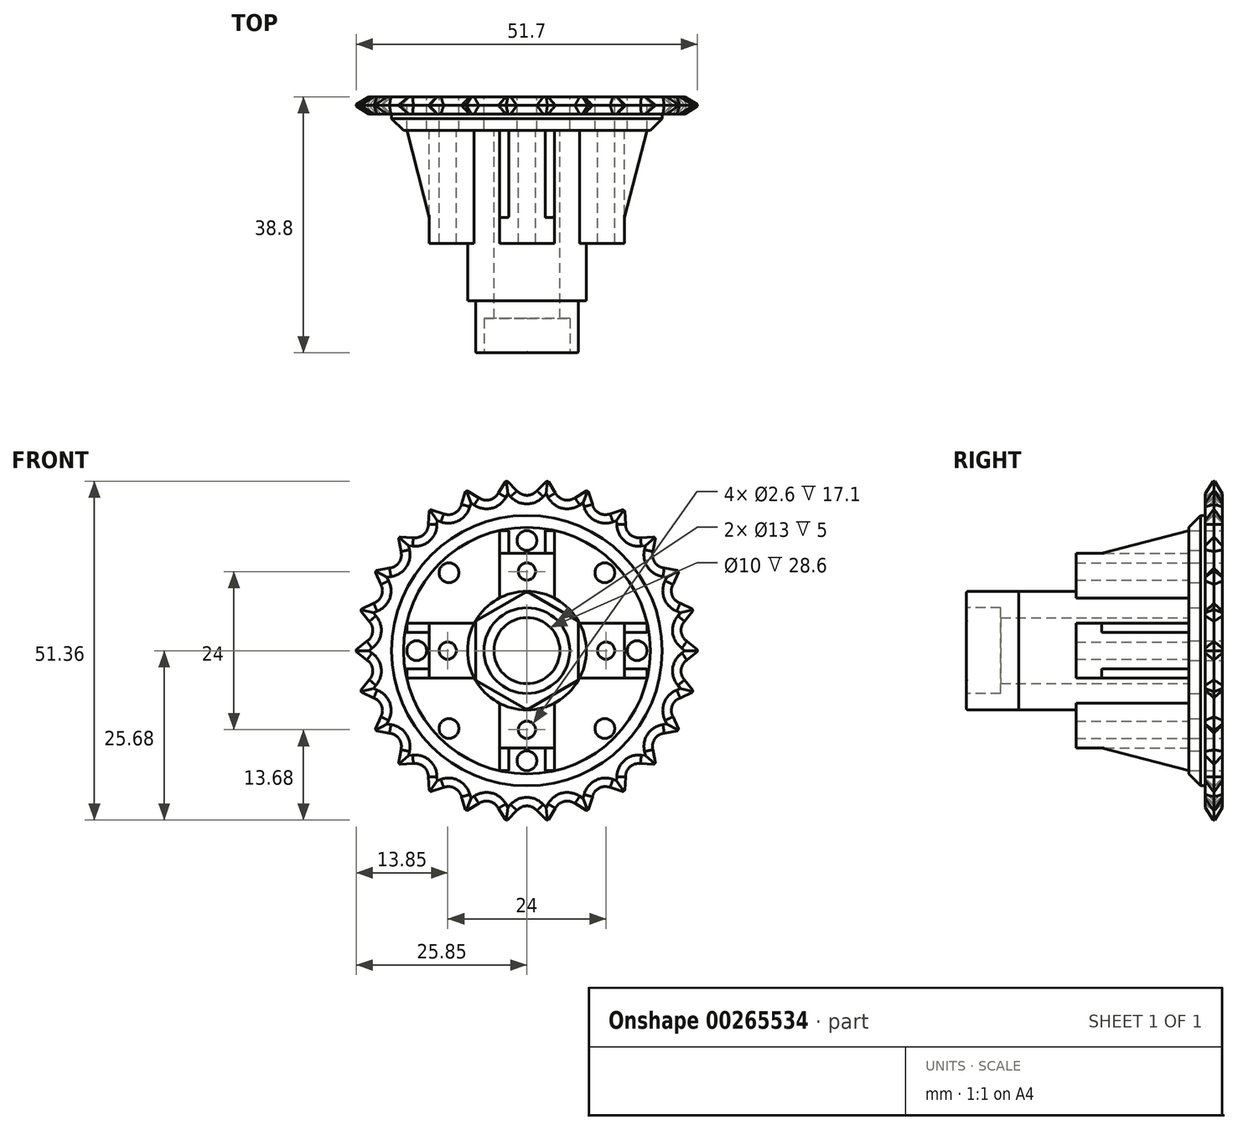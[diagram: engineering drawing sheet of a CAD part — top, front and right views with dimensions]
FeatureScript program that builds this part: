
annotation { "Feature Type Name" : "Feature", "Feature Type Description" : "" }
export const myFeature = defineFeature(function(context is Context, id is Id, definition is map)
    precondition{}
    {
        {
            var Q0;
            Q0=qCreatedBy(makeId("Front.planeOp"),FACE);
            var sketch = newSketch(context, id + "F0", { "sketchPlane" : qUnion([Q0])});
            skCircle(sketch, "E0", {"center": v(0, 0) * mm, "radius": 22.85 * mm});
            skSolve(sketch);
        }
        {
            var Q0;
            Q0=makeQuery(id+"F0.imprint","IMPRINT",FACE,{"disambiguationData":[TD([[makeQuery(id+"F0.imprint","IMPRINT",EDGE,{"derivedFrom":sQuery(id+"F0.wireOp",EDGE,"E0")}),1.0]])]});
            extrude(context, id + "F1", {"entities" : qUnion([Q0]), "depth" : 2.6 * mm});
        }
        {
            var Q0;
            Q0=qCreatedBy(makeId("Front.planeOp"),FACE);
            var sketch = newSketch(context, id + "F2", { "sketchPlane" : qUnion([Q0])});
            skCircle(sketch, "E1", {"center": v(0, 0) * mm, "radius": 25.85 * mm});
            skLineSegment(sketch, "E2", {"start": v(0, 0) * mm, "end": v(0, 38.8) * mm, "construction": true});
            skPoint(sketch, "E3.center", {"position": v(0, 0.05) * mm});
            skLineSegment(sketch, "E4", {"start": v(0, 25.85) * mm, "end": v(-3.12, 25.85) * mm, "construction": true});
            skLineSegment(sketch, "E5", {"start": v(0, 25.85) * mm, "end": v(3.12, 25.85) * mm, "construction": true});
            skLineSegment(sketch, "E6", {"start": v(-3.12, 25.85) * mm, "end": v(-3.12, 22.64) * mm, "construction": true});
            skLineSegment(sketch, "E7", {"start": v(3.12, 25.85) * mm, "end": v(3.12, 22.64) * mm, "construction": true});
            skLineSegment(sketch, "E8", {"start": v(-3.12, 25.85) * mm, "end": v(0, 22.73) * mm});
            skLineSegment(sketch, "E9", {"start": v(3.12, 25.85) * mm, "end": v(0, 22.73) * mm});
            skLineSegment(sketch, "E10", {"start": v(-3.12, 24.24) * mm, "end": v(3.12, 24.24) * mm, "construction": true});
            skArc(sketch, "E11", {"start": v(-1.52, 24.24) * mm, "mid": v(0, 23.55) * mm, "end": v(1.52, 24.24) * mm});
            skLineSegment(sketch, "E12.1.0", {"start": v(-9.22, 24.35) * mm, "end": v(-5.44, 22.07) * mm});
            skArc(sketch, "E12.1.1", {"start": v(-7.27, 23.18) * mm, "mid": v(-5.64, 22.87) * mm, "end": v(-4.33, 23.9) * mm});
            skLineSegment(sketch, "E12.1.2", {"start": v(-3.15, 25.85) * mm, "end": v(-5.44, 22.07) * mm});
            skLineSegment(sketch, "E12.2.0", {"start": v(-14.78, 21.44) * mm, "end": v(-10.56, 20.12) * mm});
            skArc(sketch, "E12.2.1", {"start": v(-12.6, 20.76) * mm, "mid": v(-10.94, 20.85) * mm, "end": v(-9.92, 22.17) * mm});
            skLineSegment(sketch, "E12.2.2", {"start": v(-9.25, 24.34) * mm, "end": v(-10.56, 20.12) * mm});
            skLineSegment(sketch, "E12.3.0", {"start": v(-19.48, 17.28) * mm, "end": v(-15.07, 17.01) * mm});
            skArc(sketch, "E12.3.1", {"start": v(-17.21, 17.14) * mm, "mid": v(-15.62, 17.63) * mm, "end": v(-14.94, 19.15) * mm});
            skLineSegment(sketch, "E12.3.2", {"start": v(-14.8, 21.42) * mm, "end": v(-15.07, 17.01) * mm});
            skLineSegment(sketch, "E12.4.0", {"start": v(-23.05, 12.11) * mm, "end": v(-18.7, 12.91) * mm});
            skArc(sketch, "E12.4.1", {"start": v(-20.81, 12.52) * mm, "mid": v(-19.38, 13.38) * mm, "end": v(-19.1, 15.02) * mm});
            skLineSegment(sketch, "E12.4.2", {"start": v(-19.5, 17.26) * mm, "end": v(-18.7, 12.91) * mm});
            skLineSegment(sketch, "E12.5.0", {"start": v(-25.28, 6.25) * mm, "end": v(-21.25, 8.06) * mm});
            skArc(sketch, "E12.5.1", {"start": v(-23.2, 7.18) * mm, "mid": v(-22.02, 8.35) * mm, "end": v(-22.13, 10.01) * mm});
            skLineSegment(sketch, "E12.5.2", {"start": v(-23.06, 12.09) * mm, "end": v(-21.25, 8.06) * mm});
            skLineSegment(sketch, "E12.6.0", {"start": v(-26.04, 0.02) * mm, "end": v(-22.56, 2.74) * mm});
            skArc(sketch, "E12.6.1", {"start": v(-24.25, 1.42) * mm, "mid": v(-23.38, 2.84) * mm, "end": v(-23.88, 4.43) * mm});
            skLineSegment(sketch, "E12.6.2", {"start": v(-25.29, 6.22) * mm, "end": v(-22.56, 2.74) * mm});
            skLineSegment(sketch, "E12.7.0", {"start": v(-25.29, -6.22) * mm, "end": v(-22.56, -2.74) * mm});
            skArc(sketch, "E12.7.1", {"start": v(-23.88, -4.43) * mm, "mid": v(-23.38, -2.84) * mm, "end": v(-24.25, -1.42) * mm});
            skLineSegment(sketch, "E12.7.2", {"start": v(-26.04, -0.02) * mm, "end": v(-22.56, -2.74) * mm});
            skLineSegment(sketch, "E12.8.0", {"start": v(-23.06, -12.09) * mm, "end": v(-21.25, -8.06) * mm});
            skArc(sketch, "E12.8.1", {"start": v(-22.13, -10.01) * mm, "mid": v(-22.02, -8.35) * mm, "end": v(-23.2, -7.18) * mm});
            skLineSegment(sketch, "E12.8.2", {"start": v(-25.28, -6.25) * mm, "end": v(-21.25, -8.06) * mm});
            skLineSegment(sketch, "E12.9.0", {"start": v(-19.5, -17.26) * mm, "end": v(-18.7, -12.91) * mm});
            skArc(sketch, "E12.9.1", {"start": v(-19.1, -15.02) * mm, "mid": v(-19.38, -13.38) * mm, "end": v(-20.81, -12.52) * mm});
            skLineSegment(sketch, "E12.9.2", {"start": v(-23.05, -12.11) * mm, "end": v(-18.7, -12.91) * mm});
            skLineSegment(sketch, "E12.10.0", {"start": v(-14.8, -21.42) * mm, "end": v(-15.07, -17.01) * mm});
            skArc(sketch, "E12.10.1", {"start": v(-14.94, -19.15) * mm, "mid": v(-15.62, -17.63) * mm, "end": v(-17.21, -17.14) * mm});
            skLineSegment(sketch, "E12.10.2", {"start": v(-19.48, -17.28) * mm, "end": v(-15.07, -17.01) * mm});
            skLineSegment(sketch, "E12.11.0", {"start": v(-9.25, -24.34) * mm, "end": v(-10.56, -20.12) * mm});
            skArc(sketch, "E12.11.1", {"start": v(-9.92, -22.17) * mm, "mid": v(-10.94, -20.85) * mm, "end": v(-12.6, -20.76) * mm});
            skLineSegment(sketch, "E12.11.2", {"start": v(-14.78, -21.44) * mm, "end": v(-10.56, -20.12) * mm});
            skLineSegment(sketch, "E12.12.0", {"start": v(-3.15, -25.85) * mm, "end": v(-5.44, -22.07) * mm});
            skArc(sketch, "E12.12.1", {"start": v(-4.33, -23.9) * mm, "mid": v(-5.64, -22.87) * mm, "end": v(-7.27, -23.18) * mm});
            skLineSegment(sketch, "E12.12.2", {"start": v(-9.22, -24.35) * mm, "end": v(-5.44, -22.07) * mm});
            skLineSegment(sketch, "E12.13.0", {"start": v(3.12, -25.85) * mm, "end": v(0, -22.73) * mm});
            skArc(sketch, "E12.13.1", {"start": v(1.52, -24.24) * mm, "mid": v(0, -23.55) * mm, "end": v(-1.52, -24.24) * mm});
            skLineSegment(sketch, "E12.13.2", {"start": v(-3.12, -25.85) * mm, "end": v(0, -22.73) * mm});
            skLineSegment(sketch, "E12.14.0", {"start": v(9.22, -24.35) * mm, "end": v(5.44, -22.07) * mm});
            skArc(sketch, "E12.14.1", {"start": v(7.27, -23.18) * mm, "mid": v(5.64, -22.87) * mm, "end": v(4.33, -23.9) * mm});
            skLineSegment(sketch, "E12.14.2", {"start": v(3.15, -25.85) * mm, "end": v(5.44, -22.07) * mm});
            skLineSegment(sketch, "E12.15.0", {"start": v(14.78, -21.44) * mm, "end": v(10.56, -20.12) * mm});
            skArc(sketch, "E12.15.1", {"start": v(12.6, -20.76) * mm, "mid": v(10.94, -20.85) * mm, "end": v(9.92, -22.17) * mm});
            skLineSegment(sketch, "E12.15.2", {"start": v(9.25, -24.34) * mm, "end": v(10.56, -20.12) * mm});
            skLineSegment(sketch, "E12.16.0", {"start": v(19.48, -17.28) * mm, "end": v(15.07, -17.01) * mm});
            skArc(sketch, "E12.16.1", {"start": v(17.21, -17.14) * mm, "mid": v(15.62, -17.63) * mm, "end": v(14.94, -19.15) * mm});
            skLineSegment(sketch, "E12.16.2", {"start": v(14.8, -21.42) * mm, "end": v(15.07, -17.01) * mm});
            skLineSegment(sketch, "E12.17.0", {"start": v(23.05, -12.11) * mm, "end": v(18.7, -12.91) * mm});
            skArc(sketch, "E12.17.1", {"start": v(20.81, -12.52) * mm, "mid": v(19.38, -13.38) * mm, "end": v(19.1, -15.02) * mm});
            skLineSegment(sketch, "E12.17.2", {"start": v(19.5, -17.26) * mm, "end": v(18.7, -12.91) * mm});
            skLineSegment(sketch, "E12.18.0", {"start": v(25.28, -6.25) * mm, "end": v(21.25, -8.06) * mm});
            skArc(sketch, "E12.18.1", {"start": v(23.2, -7.18) * mm, "mid": v(22.02, -8.35) * mm, "end": v(22.13, -10.01) * mm});
            skLineSegment(sketch, "E12.18.2", {"start": v(23.06, -12.09) * mm, "end": v(21.25, -8.06) * mm});
            skLineSegment(sketch, "E12.19.0", {"start": v(26.04, -0.02) * mm, "end": v(22.56, -2.74) * mm});
            skArc(sketch, "E12.19.1", {"start": v(24.25, -1.42) * mm, "mid": v(23.38, -2.84) * mm, "end": v(23.88, -4.43) * mm});
            skLineSegment(sketch, "E12.19.2", {"start": v(25.29, -6.22) * mm, "end": v(22.56, -2.74) * mm});
            skLineSegment(sketch, "E12.20.0", {"start": v(25.29, 6.22) * mm, "end": v(22.56, 2.74) * mm});
            skArc(sketch, "E12.20.1", {"start": v(23.88, 4.43) * mm, "mid": v(23.38, 2.84) * mm, "end": v(24.25, 1.42) * mm});
            skLineSegment(sketch, "E12.20.2", {"start": v(26.04, 0.02) * mm, "end": v(22.56, 2.74) * mm});
            skLineSegment(sketch, "E12.21.0", {"start": v(23.06, 12.09) * mm, "end": v(21.25, 8.06) * mm});
            skArc(sketch, "E12.21.1", {"start": v(22.13, 10.01) * mm, "mid": v(22.02, 8.35) * mm, "end": v(23.2, 7.18) * mm});
            skLineSegment(sketch, "E12.21.2", {"start": v(25.28, 6.25) * mm, "end": v(21.25, 8.06) * mm});
            skLineSegment(sketch, "E12.22.0", {"start": v(19.5, 17.26) * mm, "end": v(18.7, 12.91) * mm});
            skArc(sketch, "E12.22.1", {"start": v(19.1, 15.02) * mm, "mid": v(19.38, 13.38) * mm, "end": v(20.81, 12.52) * mm});
            skLineSegment(sketch, "E12.22.2", {"start": v(23.05, 12.11) * mm, "end": v(18.7, 12.91) * mm});
            skLineSegment(sketch, "E12.23.0", {"start": v(14.8, 21.42) * mm, "end": v(15.07, 17.01) * mm});
            skArc(sketch, "E12.23.1", {"start": v(14.94, 19.15) * mm, "mid": v(15.62, 17.63) * mm, "end": v(17.21, 17.14) * mm});
            skLineSegment(sketch, "E12.23.2", {"start": v(19.48, 17.28) * mm, "end": v(15.07, 17.01) * mm});
            skLineSegment(sketch, "E12.24.0", {"start": v(9.25, 24.34) * mm, "end": v(10.56, 20.12) * mm});
            skArc(sketch, "E12.24.1", {"start": v(9.92, 22.17) * mm, "mid": v(10.94, 20.85) * mm, "end": v(12.6, 20.76) * mm});
            skLineSegment(sketch, "E12.24.2", {"start": v(14.78, 21.44) * mm, "end": v(10.56, 20.12) * mm});
            skLineSegment(sketch, "E12.25.0", {"start": v(3.15, 25.85) * mm, "end": v(5.44, 22.07) * mm});
            skArc(sketch, "E12.25.1", {"start": v(4.33, 23.9) * mm, "mid": v(5.64, 22.87) * mm, "end": v(7.27, 23.18) * mm});
            skLineSegment(sketch, "E12.25.2", {"start": v(9.22, 24.35) * mm, "end": v(5.44, 22.07) * mm});
            skSolve(sketch);
        }
        {
            var Q0;
            {var subQ21=sQuery(id+"F2.wireOp",EDGE,"E1");var subQ92=sQuery(id+"F2.wireOp",EDGE,"E12.20.0");var subQ115=makeQuery(id+"F2.imprint","INTERSECT",VERTEX,{"derivedFrom":[subQ21,subQ92]});Q0=makeQuery(id+"F2.imprint","IMPRINT",FACE,{"disambiguationData":[TD([[makeQuery(id+"F2.imprint","IMPRINT",EDGE,{"disambiguationData":[TD([[subQ115,-1.0]])],"derivedFrom":subQ21}),1.0]])]});}
            var Q1;
            {var subQ0=sQuery(id+"F2.wireOp",EDGE,"E12.1.2");var subQ1=sQuery(id+"F2.wireOp",EDGE,"E12.1.0");var subQ2=makeQuery(id+"F2.imprint","INTERSECT",VERTEX,{"derivedFrom":[subQ1,subQ0]});Q1=makeQuery(id+"F2.imprint","IMPRINT",FACE,{"disambiguationData":[TD([[makeQuery(id+"F2.imprint","IMPRINT",EDGE,{"disambiguationData":[TD([[subQ2,1.0]])],"derivedFrom":subQ1}),1.0]])]});}
            var Q2;
            {var subQ0=sQuery(id+"F2.wireOp",EDGE,"E9");var subQ1=sQuery(id+"F2.wireOp",EDGE,"E8");var subQ2=makeQuery(id+"F2.imprint","INTERSECT",VERTEX,{"derivedFrom":[subQ1,subQ0]});Q2=makeQuery(id+"F2.imprint","IMPRINT",FACE,{"disambiguationData":[TD([[makeQuery(id+"F2.imprint","IMPRINT",EDGE,{"disambiguationData":[TD([[subQ2,1.0]])],"derivedFrom":subQ1}),1.0]])]});}
            var Q3;
            {var subQ0=sQuery(id+"F2.wireOp",EDGE,"E12.25.2");var subQ1=sQuery(id+"F2.wireOp",EDGE,"E12.25.0");var subQ2=makeQuery(id+"F2.imprint","INTERSECT",VERTEX,{"derivedFrom":[subQ1,subQ0]});Q3=makeQuery(id+"F2.imprint","IMPRINT",FACE,{"disambiguationData":[TD([[makeQuery(id+"F2.imprint","IMPRINT",EDGE,{"disambiguationData":[TD([[subQ2,1.0]])],"derivedFrom":subQ1}),1.0]])]});}
            var Q4;
            {var subQ0=sQuery(id+"F2.wireOp",EDGE,"E12.24.2");var subQ1=sQuery(id+"F2.wireOp",EDGE,"E12.24.0");var subQ2=makeQuery(id+"F2.imprint","INTERSECT",VERTEX,{"derivedFrom":[subQ1,subQ0]});Q4=makeQuery(id+"F2.imprint","IMPRINT",FACE,{"disambiguationData":[TD([[makeQuery(id+"F2.imprint","IMPRINT",EDGE,{"disambiguationData":[TD([[subQ2,1.0]])],"derivedFrom":subQ1}),1.0]])]});}
            var Q5;
            {var subQ0=sQuery(id+"F2.wireOp",EDGE,"E12.23.2");var subQ1=sQuery(id+"F2.wireOp",EDGE,"E12.23.0");var subQ2=makeQuery(id+"F2.imprint","INTERSECT",VERTEX,{"derivedFrom":[subQ1,subQ0]});Q5=makeQuery(id+"F2.imprint","IMPRINT",FACE,{"disambiguationData":[TD([[makeQuery(id+"F2.imprint","IMPRINT",EDGE,{"disambiguationData":[TD([[subQ2,1.0]])],"derivedFrom":subQ1}),1.0]])]});}
            var Q6;
            {var subQ0=sQuery(id+"F2.wireOp",EDGE,"E12.22.2");var subQ1=sQuery(id+"F2.wireOp",EDGE,"E12.22.0");var subQ2=makeQuery(id+"F2.imprint","INTERSECT",VERTEX,{"derivedFrom":[subQ1,subQ0]});Q6=makeQuery(id+"F2.imprint","IMPRINT",FACE,{"disambiguationData":[TD([[makeQuery(id+"F2.imprint","IMPRINT",EDGE,{"disambiguationData":[TD([[subQ2,1.0]])],"derivedFrom":subQ1}),1.0]])]});}
            var Q7;
            {var subQ0=sQuery(id+"F2.wireOp",EDGE,"E12.2.2");var subQ1=sQuery(id+"F2.wireOp",EDGE,"E12.2.0");var subQ2=makeQuery(id+"F2.imprint","INTERSECT",VERTEX,{"derivedFrom":[subQ1,subQ0]});Q7=makeQuery(id+"F2.imprint","IMPRINT",FACE,{"disambiguationData":[TD([[makeQuery(id+"F2.imprint","IMPRINT",EDGE,{"disambiguationData":[TD([[subQ2,1.0]])],"derivedFrom":subQ1}),1.0]])]});}
            var Q8;
            {var subQ0=sQuery(id+"F2.wireOp",EDGE,"E12.3.2");var subQ1=sQuery(id+"F2.wireOp",EDGE,"E12.3.0");var subQ2=makeQuery(id+"F2.imprint","INTERSECT",VERTEX,{"derivedFrom":[subQ1,subQ0]});Q8=makeQuery(id+"F2.imprint","IMPRINT",FACE,{"disambiguationData":[TD([[makeQuery(id+"F2.imprint","IMPRINT",EDGE,{"disambiguationData":[TD([[subQ2,1.0]])],"derivedFrom":subQ1}),1.0]])]});}
            var Q9;
            {var subQ0=sQuery(id+"F2.wireOp",EDGE,"E12.4.2");var subQ1=sQuery(id+"F2.wireOp",EDGE,"E12.4.0");var subQ2=makeQuery(id+"F2.imprint","INTERSECT",VERTEX,{"derivedFrom":[subQ1,subQ0]});Q9=makeQuery(id+"F2.imprint","IMPRINT",FACE,{"disambiguationData":[TD([[makeQuery(id+"F2.imprint","IMPRINT",EDGE,{"disambiguationData":[TD([[subQ2,1.0]])],"derivedFrom":subQ1}),1.0]])]});}
            var Q10;
            {var subQ0=sQuery(id+"F2.wireOp",EDGE,"E12.5.2");var subQ1=sQuery(id+"F2.wireOp",EDGE,"E12.5.0");var subQ2=makeQuery(id+"F2.imprint","INTERSECT",VERTEX,{"derivedFrom":[subQ1,subQ0]});Q10=makeQuery(id+"F2.imprint","IMPRINT",FACE,{"disambiguationData":[TD([[makeQuery(id+"F2.imprint","IMPRINT",EDGE,{"disambiguationData":[TD([[subQ2,1.0]])],"derivedFrom":subQ1}),1.0]])]});}
            var Q11;
            {var subQ0=sQuery(id+"F2.wireOp",EDGE,"E12.6.2");var subQ1=sQuery(id+"F2.wireOp",EDGE,"E12.6.0");var subQ2=makeQuery(id+"F2.imprint","INTERSECT",VERTEX,{"derivedFrom":[subQ1,subQ0]});Q11=makeQuery(id+"F2.imprint","IMPRINT",FACE,{"disambiguationData":[TD([[makeQuery(id+"F2.imprint","IMPRINT",EDGE,{"disambiguationData":[TD([[subQ2,1.0]])],"derivedFrom":subQ1}),1.0]])]});}
            var Q12;
            {var subQ0=sQuery(id+"F2.wireOp",EDGE,"E12.7.2");var subQ1=sQuery(id+"F2.wireOp",EDGE,"E12.7.0");var subQ2=makeQuery(id+"F2.imprint","INTERSECT",VERTEX,{"derivedFrom":[subQ1,subQ0]});Q12=makeQuery(id+"F2.imprint","IMPRINT",FACE,{"disambiguationData":[TD([[makeQuery(id+"F2.imprint","IMPRINT",EDGE,{"disambiguationData":[TD([[subQ2,1.0]])],"derivedFrom":subQ1}),1.0]])]});}
            var Q13;
            {var subQ0=sQuery(id+"F2.wireOp",EDGE,"E12.8.2");var subQ1=sQuery(id+"F2.wireOp",EDGE,"E12.8.0");var subQ2=makeQuery(id+"F2.imprint","INTERSECT",VERTEX,{"derivedFrom":[subQ1,subQ0]});Q13=makeQuery(id+"F2.imprint","IMPRINT",FACE,{"disambiguationData":[TD([[makeQuery(id+"F2.imprint","IMPRINT",EDGE,{"disambiguationData":[TD([[subQ2,1.0]])],"derivedFrom":subQ1}),1.0]])]});}
            var Q14;
            {var subQ0=sQuery(id+"F2.wireOp",EDGE,"E12.9.2");var subQ1=sQuery(id+"F2.wireOp",EDGE,"E12.9.0");var subQ2=makeQuery(id+"F2.imprint","INTERSECT",VERTEX,{"derivedFrom":[subQ1,subQ0]});Q14=makeQuery(id+"F2.imprint","IMPRINT",FACE,{"disambiguationData":[TD([[makeQuery(id+"F2.imprint","IMPRINT",EDGE,{"disambiguationData":[TD([[subQ2,1.0]])],"derivedFrom":subQ1}),1.0]])]});}
            var Q15;
            {var subQ0=sQuery(id+"F2.wireOp",EDGE,"E12.10.2");var subQ1=sQuery(id+"F2.wireOp",EDGE,"E12.10.0");var subQ2=makeQuery(id+"F2.imprint","INTERSECT",VERTEX,{"derivedFrom":[subQ1,subQ0]});Q15=makeQuery(id+"F2.imprint","IMPRINT",FACE,{"disambiguationData":[TD([[makeQuery(id+"F2.imprint","IMPRINT",EDGE,{"disambiguationData":[TD([[subQ2,1.0]])],"derivedFrom":subQ1}),1.0]])]});}
            var Q16;
            {var subQ0=sQuery(id+"F2.wireOp",EDGE,"E12.11.2");var subQ1=sQuery(id+"F2.wireOp",EDGE,"E12.11.0");var subQ2=makeQuery(id+"F2.imprint","INTERSECT",VERTEX,{"derivedFrom":[subQ1,subQ0]});Q16=makeQuery(id+"F2.imprint","IMPRINT",FACE,{"disambiguationData":[TD([[makeQuery(id+"F2.imprint","IMPRINT",EDGE,{"disambiguationData":[TD([[subQ2,1.0]])],"derivedFrom":subQ1}),1.0]])]});}
            var Q17;
            {var subQ0=sQuery(id+"F2.wireOp",EDGE,"E12.12.2");var subQ1=sQuery(id+"F2.wireOp",EDGE,"E12.12.0");var subQ2=makeQuery(id+"F2.imprint","INTERSECT",VERTEX,{"derivedFrom":[subQ1,subQ0]});Q17=makeQuery(id+"F2.imprint","IMPRINT",FACE,{"disambiguationData":[TD([[makeQuery(id+"F2.imprint","IMPRINT",EDGE,{"disambiguationData":[TD([[subQ2,1.0]])],"derivedFrom":subQ1}),1.0]])]});}
            var Q18;
            {var subQ0=sQuery(id+"F2.wireOp",EDGE,"E12.13.2");var subQ1=sQuery(id+"F2.wireOp",EDGE,"E12.13.0");var subQ2=makeQuery(id+"F2.imprint","INTERSECT",VERTEX,{"derivedFrom":[subQ1,subQ0]});Q18=makeQuery(id+"F2.imprint","IMPRINT",FACE,{"disambiguationData":[TD([[makeQuery(id+"F2.imprint","IMPRINT",EDGE,{"disambiguationData":[TD([[subQ2,1.0]])],"derivedFrom":subQ1}),1.0]])]});}
            var Q19;
            {var subQ0=sQuery(id+"F2.wireOp",EDGE,"E12.14.2");var subQ1=sQuery(id+"F2.wireOp",EDGE,"E12.14.0");var subQ2=makeQuery(id+"F2.imprint","INTERSECT",VERTEX,{"derivedFrom":[subQ1,subQ0]});Q19=makeQuery(id+"F2.imprint","IMPRINT",FACE,{"disambiguationData":[TD([[makeQuery(id+"F2.imprint","IMPRINT",EDGE,{"disambiguationData":[TD([[subQ2,1.0]])],"derivedFrom":subQ1}),1.0]])]});}
            var Q20;
            {var subQ0=sQuery(id+"F2.wireOp",EDGE,"E12.15.2");var subQ1=sQuery(id+"F2.wireOp",EDGE,"E12.15.0");var subQ2=makeQuery(id+"F2.imprint","INTERSECT",VERTEX,{"derivedFrom":[subQ1,subQ0]});Q20=makeQuery(id+"F2.imprint","IMPRINT",FACE,{"disambiguationData":[TD([[makeQuery(id+"F2.imprint","IMPRINT",EDGE,{"disambiguationData":[TD([[subQ2,1.0]])],"derivedFrom":subQ1}),1.0]])]});}
            var Q21;
            {var subQ0=sQuery(id+"F2.wireOp",EDGE,"E12.16.2");var subQ1=sQuery(id+"F2.wireOp",EDGE,"E12.16.0");var subQ2=makeQuery(id+"F2.imprint","INTERSECT",VERTEX,{"derivedFrom":[subQ1,subQ0]});Q21=makeQuery(id+"F2.imprint","IMPRINT",FACE,{"disambiguationData":[TD([[makeQuery(id+"F2.imprint","IMPRINT",EDGE,{"disambiguationData":[TD([[subQ2,1.0]])],"derivedFrom":subQ1}),1.0]])]});}
            var Q22;
            {var subQ0=sQuery(id+"F2.wireOp",EDGE,"E12.17.2");var subQ1=sQuery(id+"F2.wireOp",EDGE,"E12.17.0");var subQ2=makeQuery(id+"F2.imprint","INTERSECT",VERTEX,{"derivedFrom":[subQ1,subQ0]});Q22=makeQuery(id+"F2.imprint","IMPRINT",FACE,{"disambiguationData":[TD([[makeQuery(id+"F2.imprint","IMPRINT",EDGE,{"disambiguationData":[TD([[subQ2,1.0]])],"derivedFrom":subQ1}),1.0]])]});}
            var Q23;
            {var subQ0=sQuery(id+"F2.wireOp",EDGE,"E12.18.2");var subQ1=sQuery(id+"F2.wireOp",EDGE,"E12.18.0");var subQ2=makeQuery(id+"F2.imprint","INTERSECT",VERTEX,{"derivedFrom":[subQ1,subQ0]});Q23=makeQuery(id+"F2.imprint","IMPRINT",FACE,{"disambiguationData":[TD([[makeQuery(id+"F2.imprint","IMPRINT",EDGE,{"disambiguationData":[TD([[subQ2,1.0]])],"derivedFrom":subQ1}),1.0]])]});}
            var Q24;
            {var subQ0=sQuery(id+"F2.wireOp",EDGE,"E12.19.2");var subQ1=sQuery(id+"F2.wireOp",EDGE,"E12.19.0");var subQ2=makeQuery(id+"F2.imprint","INTERSECT",VERTEX,{"derivedFrom":[subQ1,subQ0]});Q24=makeQuery(id+"F2.imprint","IMPRINT",FACE,{"disambiguationData":[TD([[makeQuery(id+"F2.imprint","IMPRINT",EDGE,{"disambiguationData":[TD([[subQ2,1.0]])],"derivedFrom":subQ1}),1.0]])]});}
            var Q25;
            {var subQ0=sQuery(id+"F2.wireOp",EDGE,"E12.20.2");var subQ1=sQuery(id+"F2.wireOp",EDGE,"E12.20.0");var subQ2=makeQuery(id+"F2.imprint","INTERSECT",VERTEX,{"derivedFrom":[subQ1,subQ0]});Q25=makeQuery(id+"F2.imprint","IMPRINT",FACE,{"disambiguationData":[TD([[makeQuery(id+"F2.imprint","IMPRINT",EDGE,{"disambiguationData":[TD([[subQ2,1.0]])],"derivedFrom":subQ1}),1.0]])]});}
            var Q26;
            {var subQ0=sQuery(id+"F2.wireOp",EDGE,"E12.21.2");var subQ1=sQuery(id+"F2.wireOp",EDGE,"E12.21.0");var subQ2=makeQuery(id+"F2.imprint","INTERSECT",VERTEX,{"derivedFrom":[subQ1,subQ0]});Q26=makeQuery(id+"F2.imprint","IMPRINT",FACE,{"disambiguationData":[TD([[makeQuery(id+"F2.imprint","IMPRINT",EDGE,{"disambiguationData":[TD([[subQ2,1.0]])],"derivedFrom":subQ1}),1.0]])]});}
            extrude(context, id + "F3", {"entities" : qUnion([Q0, Q1, Q2, Q3, Q4, Q5, Q6, Q7, Q8, Q9, Q10, Q11, Q12, Q13, Q14, Q15, Q16, Q17, Q18, Q19, Q20, Q21, Q22, Q23, Q24, Q25, Q26]), "operationType" : NewBodyOperationType.ADD, "depth" : 2.6 * mm});
        }
        {
            var Q0;
            Q0=makeQuery(id+"F3.boolean.opBoolean","MERGE",FACE,{"derivedFrom":[makeQuery(id+"F1.opExtrude","CAP_FACE",FACE,{"disambiguationData":[OSD([sQuery(id+"F0.wireOp",EDGE,"E0")])],"isStart":false}),makeQuery(id+"F3.opExtrude","CAP_FACE",FACE,{"disambiguationData":[OSD([sQuery(id+"F2.wireOp",EDGE,"E1"),sQuery(id+"F2.wireOp",EDGE,"E8"),sQuery(id+"F2.wireOp",EDGE,"E9"),sQuery(id+"F2.wireOp",EDGE,"E11"),sQuery(id+"F2.wireOp",EDGE,"E12.1.0"),sQuery(id+"F2.wireOp",EDGE,"E12.1.1"),sQuery(id+"F2.wireOp",EDGE,"E12.1.2"),sQuery(id+"F2.wireOp",EDGE,"E12.2.0"),sQuery(id+"F2.wireOp",EDGE,"E12.2.1"),sQuery(id+"F2.wireOp",EDGE,"E12.2.2"),sQuery(id+"F2.wireOp",EDGE,"E12.3.0"),sQuery(id+"F2.wireOp",EDGE,"E12.3.1"),sQuery(id+"F2.wireOp",EDGE,"E12.3.2"),sQuery(id+"F2.wireOp",EDGE,"E12.4.0"),sQuery(id+"F2.wireOp",EDGE,"E12.4.1"),sQuery(id+"F2.wireOp",EDGE,"E12.4.2"),sQuery(id+"F2.wireOp",EDGE,"E12.5.0"),sQuery(id+"F2.wireOp",EDGE,"E12.5.1"),sQuery(id+"F2.wireOp",EDGE,"E12.5.2"),sQuery(id+"F2.wireOp",EDGE,"E12.6.0"),sQuery(id+"F2.wireOp",EDGE,"E12.6.1"),sQuery(id+"F2.wireOp",EDGE,"E12.6.2"),sQuery(id+"F2.wireOp",EDGE,"E12.7.0"),sQuery(id+"F2.wireOp",EDGE,"E12.7.1"),sQuery(id+"F2.wireOp",EDGE,"E12.7.2"),sQuery(id+"F2.wireOp",EDGE,"E12.8.0"),sQuery(id+"F2.wireOp",EDGE,"E12.8.1"),sQuery(id+"F2.wireOp",EDGE,"E12.8.2"),sQuery(id+"F2.wireOp",EDGE,"E12.9.0"),sQuery(id+"F2.wireOp",EDGE,"E12.9.1"),sQuery(id+"F2.wireOp",EDGE,"E12.9.2"),sQuery(id+"F2.wireOp",EDGE,"E12.10.0"),sQuery(id+"F2.wireOp",EDGE,"E12.10.1"),sQuery(id+"F2.wireOp",EDGE,"E12.10.2"),sQuery(id+"F2.wireOp",EDGE,"E12.11.0"),sQuery(id+"F2.wireOp",EDGE,"E12.11.1"),sQuery(id+"F2.wireOp",EDGE,"E12.11.2"),sQuery(id+"F2.wireOp",EDGE,"E12.12.0"),sQuery(id+"F2.wireOp",EDGE,"E12.12.1"),sQuery(id+"F2.wireOp",EDGE,"E12.12.2"),sQuery(id+"F2.wireOp",EDGE,"E12.13.0"),sQuery(id+"F2.wireOp",EDGE,"E12.13.1"),sQuery(id+"F2.wireOp",EDGE,"E12.13.2"),sQuery(id+"F2.wireOp",EDGE,"E12.14.0"),sQuery(id+"F2.wireOp",EDGE,"E12.14.1"),sQuery(id+"F2.wireOp",EDGE,"E12.14.2"),sQuery(id+"F2.wireOp",EDGE,"E12.15.0"),sQuery(id+"F2.wireOp",EDGE,"E12.15.1"),sQuery(id+"F2.wireOp",EDGE,"E12.15.2"),sQuery(id+"F2.wireOp",EDGE,"E12.16.0"),sQuery(id+"F2.wireOp",EDGE,"E12.16.1"),sQuery(id+"F2.wireOp",EDGE,"E12.16.2"),sQuery(id+"F2.wireOp",EDGE,"E12.17.0"),sQuery(id+"F2.wireOp",EDGE,"E12.17.1"),sQuery(id+"F2.wireOp",EDGE,"E12.17.2"),sQuery(id+"F2.wireOp",EDGE,"E12.18.0"),sQuery(id+"F2.wireOp",EDGE,"E12.18.1"),sQuery(id+"F2.wireOp",EDGE,"E12.18.2"),sQuery(id+"F2.wireOp",EDGE,"E12.19.0"),sQuery(id+"F2.wireOp",EDGE,"E12.19.1"),sQuery(id+"F2.wireOp",EDGE,"E12.19.2"),sQuery(id+"F2.wireOp",EDGE,"E12.20.0"),sQuery(id+"F2.wireOp",EDGE,"E12.20.1"),sQuery(id+"F2.wireOp",EDGE,"E12.20.2"),sQuery(id+"F2.wireOp",EDGE,"E12.21.0"),sQuery(id+"F2.wireOp",EDGE,"E12.21.1"),sQuery(id+"F2.wireOp",EDGE,"E12.21.2"),sQuery(id+"F2.wireOp",EDGE,"E12.22.0"),sQuery(id+"F2.wireOp",EDGE,"E12.22.1"),sQuery(id+"F2.wireOp",EDGE,"E12.22.2"),sQuery(id+"F2.wireOp",EDGE,"E12.23.0"),sQuery(id+"F2.wireOp",EDGE,"E12.23.1"),sQuery(id+"F2.wireOp",EDGE,"E12.23.2"),sQuery(id+"F2.wireOp",EDGE,"E12.24.0"),sQuery(id+"F2.wireOp",EDGE,"E12.24.1"),sQuery(id+"F2.wireOp",EDGE,"E12.24.2"),sQuery(id+"F2.wireOp",EDGE,"E12.25.0"),sQuery(id+"F2.wireOp",EDGE,"E12.25.1"),sQuery(id+"F2.wireOp",EDGE,"E12.25.2")])],"isStart":false})]});
            var sketch = newSketch(context, id + "F4", { "sketchPlane" : qUnion([Q0])});
            skCircle(sketch, "E13", {"center": v(0, 0) * mm, "radius": 20.5 * mm});
            skSolve(sketch);
        }
        {
            var Q0;
            Q0=makeQuery(id+"F3.boolean.opBoolean","MERGE",FACE,{"derivedFrom":[makeQuery(id+"F1.opExtrude","CAP_FACE",FACE,{"disambiguationData":[OSD([sQuery(id+"F0.wireOp",EDGE,"E0")])],"isStart":true}),makeQuery(id+"F3.opExtrude","CAP_FACE",FACE,{"disambiguationData":[OSD([sQuery(id+"F2.wireOp",EDGE,"E1"),sQuery(id+"F2.wireOp",EDGE,"E8"),sQuery(id+"F2.wireOp",EDGE,"E9"),sQuery(id+"F2.wireOp",EDGE,"E11"),sQuery(id+"F2.wireOp",EDGE,"E12.1.0"),sQuery(id+"F2.wireOp",EDGE,"E12.1.1"),sQuery(id+"F2.wireOp",EDGE,"E12.1.2"),sQuery(id+"F2.wireOp",EDGE,"E12.2.0"),sQuery(id+"F2.wireOp",EDGE,"E12.2.1"),sQuery(id+"F2.wireOp",EDGE,"E12.2.2"),sQuery(id+"F2.wireOp",EDGE,"E12.3.0"),sQuery(id+"F2.wireOp",EDGE,"E12.3.1"),sQuery(id+"F2.wireOp",EDGE,"E12.3.2"),sQuery(id+"F2.wireOp",EDGE,"E12.4.0"),sQuery(id+"F2.wireOp",EDGE,"E12.4.1"),sQuery(id+"F2.wireOp",EDGE,"E12.4.2"),sQuery(id+"F2.wireOp",EDGE,"E12.5.0"),sQuery(id+"F2.wireOp",EDGE,"E12.5.1"),sQuery(id+"F2.wireOp",EDGE,"E12.5.2"),sQuery(id+"F2.wireOp",EDGE,"E12.6.0"),sQuery(id+"F2.wireOp",EDGE,"E12.6.1"),sQuery(id+"F2.wireOp",EDGE,"E12.6.2"),sQuery(id+"F2.wireOp",EDGE,"E12.7.0"),sQuery(id+"F2.wireOp",EDGE,"E12.7.1"),sQuery(id+"F2.wireOp",EDGE,"E12.7.2"),sQuery(id+"F2.wireOp",EDGE,"E12.8.0"),sQuery(id+"F2.wireOp",EDGE,"E12.8.1"),sQuery(id+"F2.wireOp",EDGE,"E12.8.2"),sQuery(id+"F2.wireOp",EDGE,"E12.9.0"),sQuery(id+"F2.wireOp",EDGE,"E12.9.1"),sQuery(id+"F2.wireOp",EDGE,"E12.9.2"),sQuery(id+"F2.wireOp",EDGE,"E12.10.0"),sQuery(id+"F2.wireOp",EDGE,"E12.10.1"),sQuery(id+"F2.wireOp",EDGE,"E12.10.2"),sQuery(id+"F2.wireOp",EDGE,"E12.11.0"),sQuery(id+"F2.wireOp",EDGE,"E12.11.1"),sQuery(id+"F2.wireOp",EDGE,"E12.11.2"),sQuery(id+"F2.wireOp",EDGE,"E12.12.0"),sQuery(id+"F2.wireOp",EDGE,"E12.12.1"),sQuery(id+"F2.wireOp",EDGE,"E12.12.2"),sQuery(id+"F2.wireOp",EDGE,"E12.13.0"),sQuery(id+"F2.wireOp",EDGE,"E12.13.1"),sQuery(id+"F2.wireOp",EDGE,"E12.13.2"),sQuery(id+"F2.wireOp",EDGE,"E12.14.0"),sQuery(id+"F2.wireOp",EDGE,"E12.14.1"),sQuery(id+"F2.wireOp",EDGE,"E12.14.2"),sQuery(id+"F2.wireOp",EDGE,"E12.15.0"),sQuery(id+"F2.wireOp",EDGE,"E12.15.1"),sQuery(id+"F2.wireOp",EDGE,"E12.15.2"),sQuery(id+"F2.wireOp",EDGE,"E12.16.0"),sQuery(id+"F2.wireOp",EDGE,"E12.16.1"),sQuery(id+"F2.wireOp",EDGE,"E12.16.2"),sQuery(id+"F2.wireOp",EDGE,"E12.17.0"),sQuery(id+"F2.wireOp",EDGE,"E12.17.1"),sQuery(id+"F2.wireOp",EDGE,"E12.17.2"),sQuery(id+"F2.wireOp",EDGE,"E12.18.0"),sQuery(id+"F2.wireOp",EDGE,"E12.18.1"),sQuery(id+"F2.wireOp",EDGE,"E12.18.2"),sQuery(id+"F2.wireOp",EDGE,"E12.19.0"),sQuery(id+"F2.wireOp",EDGE,"E12.19.1"),sQuery(id+"F2.wireOp",EDGE,"E12.19.2"),sQuery(id+"F2.wireOp",EDGE,"E12.20.0"),sQuery(id+"F2.wireOp",EDGE,"E12.20.1"),sQuery(id+"F2.wireOp",EDGE,"E12.20.2"),sQuery(id+"F2.wireOp",EDGE,"E12.21.0"),sQuery(id+"F2.wireOp",EDGE,"E12.21.1"),sQuery(id+"F2.wireOp",EDGE,"E12.21.2"),sQuery(id+"F2.wireOp",EDGE,"E12.22.0"),sQuery(id+"F2.wireOp",EDGE,"E12.22.1"),sQuery(id+"F2.wireOp",EDGE,"E12.22.2"),sQuery(id+"F2.wireOp",EDGE,"E12.23.0"),sQuery(id+"F2.wireOp",EDGE,"E12.23.1"),sQuery(id+"F2.wireOp",EDGE,"E12.23.2"),sQuery(id+"F2.wireOp",EDGE,"E12.24.0"),sQuery(id+"F2.wireOp",EDGE,"E12.24.1"),sQuery(id+"F2.wireOp",EDGE,"E12.24.2"),sQuery(id+"F2.wireOp",EDGE,"E12.25.0"),sQuery(id+"F2.wireOp",EDGE,"E12.25.1"),sQuery(id+"F2.wireOp",EDGE,"E12.25.2")])],"isStart":true})]});
            chamfer(context, id + "F5", {"entities" : qUnion([Q0]), "width" : 1.3 * mm, "tangentPropagation" : true});
        }
        {
            var Q0;
            Q0=makeQuery(id+"F3.boolean.opBoolean","MERGE",FACE,{"derivedFrom":[makeQuery(id+"F1.opExtrude","CAP_FACE",FACE,{"disambiguationData":[OSD([sQuery(id+"F0.wireOp",EDGE,"E0")])],"isStart":false}),makeQuery(id+"F3.opExtrude","CAP_FACE",FACE,{"disambiguationData":[OSD([sQuery(id+"F2.wireOp",EDGE,"E1"),sQuery(id+"F2.wireOp",EDGE,"E8"),sQuery(id+"F2.wireOp",EDGE,"E9"),sQuery(id+"F2.wireOp",EDGE,"E11"),sQuery(id+"F2.wireOp",EDGE,"E12.1.0"),sQuery(id+"F2.wireOp",EDGE,"E12.1.1"),sQuery(id+"F2.wireOp",EDGE,"E12.1.2"),sQuery(id+"F2.wireOp",EDGE,"E12.2.0"),sQuery(id+"F2.wireOp",EDGE,"E12.2.1"),sQuery(id+"F2.wireOp",EDGE,"E12.2.2"),sQuery(id+"F2.wireOp",EDGE,"E12.3.0"),sQuery(id+"F2.wireOp",EDGE,"E12.3.1"),sQuery(id+"F2.wireOp",EDGE,"E12.3.2"),sQuery(id+"F2.wireOp",EDGE,"E12.4.0"),sQuery(id+"F2.wireOp",EDGE,"E12.4.1"),sQuery(id+"F2.wireOp",EDGE,"E12.4.2"),sQuery(id+"F2.wireOp",EDGE,"E12.5.0"),sQuery(id+"F2.wireOp",EDGE,"E12.5.1"),sQuery(id+"F2.wireOp",EDGE,"E12.5.2"),sQuery(id+"F2.wireOp",EDGE,"E12.6.0"),sQuery(id+"F2.wireOp",EDGE,"E12.6.1"),sQuery(id+"F2.wireOp",EDGE,"E12.6.2"),sQuery(id+"F2.wireOp",EDGE,"E12.7.0"),sQuery(id+"F2.wireOp",EDGE,"E12.7.1"),sQuery(id+"F2.wireOp",EDGE,"E12.7.2"),sQuery(id+"F2.wireOp",EDGE,"E12.8.0"),sQuery(id+"F2.wireOp",EDGE,"E12.8.1"),sQuery(id+"F2.wireOp",EDGE,"E12.8.2"),sQuery(id+"F2.wireOp",EDGE,"E12.9.0"),sQuery(id+"F2.wireOp",EDGE,"E12.9.1"),sQuery(id+"F2.wireOp",EDGE,"E12.9.2"),sQuery(id+"F2.wireOp",EDGE,"E12.10.0"),sQuery(id+"F2.wireOp",EDGE,"E12.10.1"),sQuery(id+"F2.wireOp",EDGE,"E12.10.2"),sQuery(id+"F2.wireOp",EDGE,"E12.11.0"),sQuery(id+"F2.wireOp",EDGE,"E12.11.1"),sQuery(id+"F2.wireOp",EDGE,"E12.11.2"),sQuery(id+"F2.wireOp",EDGE,"E12.12.0"),sQuery(id+"F2.wireOp",EDGE,"E12.12.1"),sQuery(id+"F2.wireOp",EDGE,"E12.12.2"),sQuery(id+"F2.wireOp",EDGE,"E12.13.0"),sQuery(id+"F2.wireOp",EDGE,"E12.13.1"),sQuery(id+"F2.wireOp",EDGE,"E12.13.2"),sQuery(id+"F2.wireOp",EDGE,"E12.14.0"),sQuery(id+"F2.wireOp",EDGE,"E12.14.1"),sQuery(id+"F2.wireOp",EDGE,"E12.14.2"),sQuery(id+"F2.wireOp",EDGE,"E12.15.0"),sQuery(id+"F2.wireOp",EDGE,"E12.15.1"),sQuery(id+"F2.wireOp",EDGE,"E12.15.2"),sQuery(id+"F2.wireOp",EDGE,"E12.16.0"),sQuery(id+"F2.wireOp",EDGE,"E12.16.1"),sQuery(id+"F2.wireOp",EDGE,"E12.16.2"),sQuery(id+"F2.wireOp",EDGE,"E12.17.0"),sQuery(id+"F2.wireOp",EDGE,"E12.17.1"),sQuery(id+"F2.wireOp",EDGE,"E12.17.2"),sQuery(id+"F2.wireOp",EDGE,"E12.18.0"),sQuery(id+"F2.wireOp",EDGE,"E12.18.1"),sQuery(id+"F2.wireOp",EDGE,"E12.18.2"),sQuery(id+"F2.wireOp",EDGE,"E12.19.0"),sQuery(id+"F2.wireOp",EDGE,"E12.19.1"),sQuery(id+"F2.wireOp",EDGE,"E12.19.2"),sQuery(id+"F2.wireOp",EDGE,"E12.20.0"),sQuery(id+"F2.wireOp",EDGE,"E12.20.1"),sQuery(id+"F2.wireOp",EDGE,"E12.20.2"),sQuery(id+"F2.wireOp",EDGE,"E12.21.0"),sQuery(id+"F2.wireOp",EDGE,"E12.21.1"),sQuery(id+"F2.wireOp",EDGE,"E12.21.2"),sQuery(id+"F2.wireOp",EDGE,"E12.22.0"),sQuery(id+"F2.wireOp",EDGE,"E12.22.1"),sQuery(id+"F2.wireOp",EDGE,"E12.22.2"),sQuery(id+"F2.wireOp",EDGE,"E12.23.0"),sQuery(id+"F2.wireOp",EDGE,"E12.23.1"),sQuery(id+"F2.wireOp",EDGE,"E12.23.2"),sQuery(id+"F2.wireOp",EDGE,"E12.24.0"),sQuery(id+"F2.wireOp",EDGE,"E12.24.1"),sQuery(id+"F2.wireOp",EDGE,"E12.24.2"),sQuery(id+"F2.wireOp",EDGE,"E12.25.0"),sQuery(id+"F2.wireOp",EDGE,"E12.25.1"),sQuery(id+"F2.wireOp",EDGE,"E12.25.2")])],"isStart":false})]});
            chamfer(context, id + "F6", {"entities" : qUnion([Q0]), "width" : 1.3 * mm, "tangentPropagation" : true});
        }
        {
            var Q0;
            Q0=makeQuery(id+"F4.imprint","IMPRINT",FACE,{"disambiguationData":[TD([[makeQuery(id+"F4.imprint","IMPRINT",EDGE,{"derivedFrom":sQuery(id+"F4.wireOp",EDGE,"E13")}),1.0]])]});
            extrude(context, id + "F7", {"entities" : qUnion([Q0]), "operationType" : NewBodyOperationType.ADD, "depth" : 2.5 * mm});
        }
        {
            var Q0;
            Q0=makeQuery(id+"F7.opExtrude","CAP_EDGE",EDGE,{"disambiguationData":[OSD([sQuery(id+"F4.wireOp",EDGE,"E13")])],"isStart":false});
            chamfer(context, id + "F8", {"entities" : qUnion([Q0]), "width" : 1.8 * mm, "tangentPropagation" : true});
        }
        {
            var Q0;
            Q0=makeQuery(id+"F3.boolean.opBoolean","MERGE",FACE,{"derivedFrom":[makeQuery(id+"F1.opExtrude","CAP_FACE",FACE,{"disambiguationData":[OSD([sQuery(id+"F0.wireOp",EDGE,"E0")])],"isStart":true}),makeQuery(id+"F3.opExtrude","CAP_FACE",FACE,{"disambiguationData":[OSD([sQuery(id+"F2.wireOp",EDGE,"E1"),sQuery(id+"F2.wireOp",EDGE,"E8"),sQuery(id+"F2.wireOp",EDGE,"E9"),sQuery(id+"F2.wireOp",EDGE,"E11"),sQuery(id+"F2.wireOp",EDGE,"E12.1.0"),sQuery(id+"F2.wireOp",EDGE,"E12.1.1"),sQuery(id+"F2.wireOp",EDGE,"E12.1.2"),sQuery(id+"F2.wireOp",EDGE,"E12.2.0"),sQuery(id+"F2.wireOp",EDGE,"E12.2.1"),sQuery(id+"F2.wireOp",EDGE,"E12.2.2"),sQuery(id+"F2.wireOp",EDGE,"E12.3.0"),sQuery(id+"F2.wireOp",EDGE,"E12.3.1"),sQuery(id+"F2.wireOp",EDGE,"E12.3.2"),sQuery(id+"F2.wireOp",EDGE,"E12.4.0"),sQuery(id+"F2.wireOp",EDGE,"E12.4.1"),sQuery(id+"F2.wireOp",EDGE,"E12.4.2"),sQuery(id+"F2.wireOp",EDGE,"E12.5.0"),sQuery(id+"F2.wireOp",EDGE,"E12.5.1"),sQuery(id+"F2.wireOp",EDGE,"E12.5.2"),sQuery(id+"F2.wireOp",EDGE,"E12.6.0"),sQuery(id+"F2.wireOp",EDGE,"E12.6.1"),sQuery(id+"F2.wireOp",EDGE,"E12.6.2"),sQuery(id+"F2.wireOp",EDGE,"E12.7.0"),sQuery(id+"F2.wireOp",EDGE,"E12.7.1"),sQuery(id+"F2.wireOp",EDGE,"E12.7.2"),sQuery(id+"F2.wireOp",EDGE,"E12.8.0"),sQuery(id+"F2.wireOp",EDGE,"E12.8.1"),sQuery(id+"F2.wireOp",EDGE,"E12.8.2"),sQuery(id+"F2.wireOp",EDGE,"E12.9.0"),sQuery(id+"F2.wireOp",EDGE,"E12.9.1"),sQuery(id+"F2.wireOp",EDGE,"E12.9.2"),sQuery(id+"F2.wireOp",EDGE,"E12.10.0"),sQuery(id+"F2.wireOp",EDGE,"E12.10.1"),sQuery(id+"F2.wireOp",EDGE,"E12.10.2"),sQuery(id+"F2.wireOp",EDGE,"E12.11.0"),sQuery(id+"F2.wireOp",EDGE,"E12.11.1"),sQuery(id+"F2.wireOp",EDGE,"E12.11.2"),sQuery(id+"F2.wireOp",EDGE,"E12.12.0"),sQuery(id+"F2.wireOp",EDGE,"E12.12.1"),sQuery(id+"F2.wireOp",EDGE,"E12.12.2"),sQuery(id+"F2.wireOp",EDGE,"E12.13.0"),sQuery(id+"F2.wireOp",EDGE,"E12.13.1"),sQuery(id+"F2.wireOp",EDGE,"E12.13.2"),sQuery(id+"F2.wireOp",EDGE,"E12.14.0"),sQuery(id+"F2.wireOp",EDGE,"E12.14.1"),sQuery(id+"F2.wireOp",EDGE,"E12.14.2"),sQuery(id+"F2.wireOp",EDGE,"E12.15.0"),sQuery(id+"F2.wireOp",EDGE,"E12.15.1"),sQuery(id+"F2.wireOp",EDGE,"E12.15.2"),sQuery(id+"F2.wireOp",EDGE,"E12.16.0"),sQuery(id+"F2.wireOp",EDGE,"E12.16.1"),sQuery(id+"F2.wireOp",EDGE,"E12.16.2"),sQuery(id+"F2.wireOp",EDGE,"E12.17.0"),sQuery(id+"F2.wireOp",EDGE,"E12.17.1"),sQuery(id+"F2.wireOp",EDGE,"E12.17.2"),sQuery(id+"F2.wireOp",EDGE,"E12.18.0"),sQuery(id+"F2.wireOp",EDGE,"E12.18.1"),sQuery(id+"F2.wireOp",EDGE,"E12.18.2"),sQuery(id+"F2.wireOp",EDGE,"E12.19.0"),sQuery(id+"F2.wireOp",EDGE,"E12.19.1"),sQuery(id+"F2.wireOp",EDGE,"E12.19.2"),sQuery(id+"F2.wireOp",EDGE,"E12.20.0"),sQuery(id+"F2.wireOp",EDGE,"E12.20.1"),sQuery(id+"F2.wireOp",EDGE,"E12.20.2"),sQuery(id+"F2.wireOp",EDGE,"E12.21.0"),sQuery(id+"F2.wireOp",EDGE,"E12.21.1"),sQuery(id+"F2.wireOp",EDGE,"E12.21.2"),sQuery(id+"F2.wireOp",EDGE,"E12.22.0"),sQuery(id+"F2.wireOp",EDGE,"E12.22.1"),sQuery(id+"F2.wireOp",EDGE,"E12.22.2"),sQuery(id+"F2.wireOp",EDGE,"E12.23.0"),sQuery(id+"F2.wireOp",EDGE,"E12.23.1"),sQuery(id+"F2.wireOp",EDGE,"E12.23.2"),sQuery(id+"F2.wireOp",EDGE,"E12.24.0"),sQuery(id+"F2.wireOp",EDGE,"E12.24.1"),sQuery(id+"F2.wireOp",EDGE,"E12.24.2"),sQuery(id+"F2.wireOp",EDGE,"E12.25.0"),sQuery(id+"F2.wireOp",EDGE,"E12.25.1"),sQuery(id+"F2.wireOp",EDGE,"E12.25.2")])],"isStart":true})]});
            var sketch = newSketch(context, id + "F9", { "sketchPlane" : qUnion([Q0])});
            skCircle(sketch, "E14", {"center": v(0, 0) * mm, "radius": 6.5 * mm});
            skCircle(sketch, "E15", {"center": v(0, 0) * mm, "radius": 5 * mm});
            skPoint(sketch, "E16.endSnap0", {"position": v(0, 22.25) * mm});
            skLineSegment(sketch, "E17", {"start": v(0, 6.5) * mm, "end": v(0, 16.7) * mm, "construction": true});
            skCircle(sketch, "E18", {"center": v(0, 16.7) * mm, "radius": 1.5 * mm});
            skCircle(sketch, "E19.1.0", {"center": v(-11.8, 11.8) * mm, "radius": 1.5 * mm});
            skCircle(sketch, "E19.2.0", {"center": v(-16.7, 0) * mm, "radius": 1.5 * mm});
            skCircle(sketch, "E19.3.0", {"center": v(-11.8, -11.8) * mm, "radius": 1.5 * mm});
            skCircle(sketch, "E19.4.0", {"center": v(0, -16.7) * mm, "radius": 1.5 * mm});
            skCircle(sketch, "E19.5.0", {"center": v(11.8, -11.8) * mm, "radius": 1.5 * mm});
            skCircle(sketch, "E19.6.0", {"center": v(16.7, 0) * mm, "radius": 1.5 * mm});
            skCircle(sketch, "E19.7.0", {"center": v(11.8, 11.8) * mm, "radius": 1.5 * mm});
            skLineSegment(sketch, "E20", {"start": v(-16.7, 0) * mm, "end": v(-27, 0) * mm, "construction": true});
            skLineSegment(sketch, "E21", {"start": v(0, -16.7) * mm, "end": v(0, -26.37) * mm, "construction": true});
            skLineSegment(sketch, "E22", {"start": v(16.7, 0) * mm, "end": v(31.56, 0) * mm, "construction": true});
            skSolve(sketch);
        }
        {
            var Q0;
            Q0=makeQuery(id+"F9.imprint","IMPRINT",FACE,{"disambiguationData":[TD([[makeQuery(id+"F9.imprint","IMPRINT",EDGE,{"derivedFrom":sQuery(id+"F9.wireOp",EDGE,"E15")}),1.0]])]});
            var Q1;
            Q1=makeQuery(id+"F9.imprint","IMPRINT",FACE,{"disambiguationData":[TD([[makeQuery(id+"F9.imprint","IMPRINT",EDGE,{"derivedFrom":sQuery(id+"F9.wireOp",EDGE,"E19.1.0")}),1.0]])]});
            var Q2;
            Q2=makeQuery(id+"F9.imprint","IMPRINT",FACE,{"disambiguationData":[TD([[makeQuery(id+"F9.imprint","IMPRINT",EDGE,{"derivedFrom":sQuery(id+"F9.wireOp",EDGE,"E18")}),1.0]])]});
            var Q3;
            Q3=makeQuery(id+"F9.imprint","IMPRINT",FACE,{"disambiguationData":[TD([[makeQuery(id+"F9.imprint","IMPRINT",EDGE,{"derivedFrom":sQuery(id+"F9.wireOp",EDGE,"E19.2.0")}),1.0]])]});
            var Q4;
            Q4=makeQuery(id+"F9.imprint","IMPRINT",FACE,{"disambiguationData":[TD([[makeQuery(id+"F9.imprint","IMPRINT",EDGE,{"derivedFrom":sQuery(id+"F9.wireOp",EDGE,"E19.3.0")}),1.0]])]});
            var Q5;
            Q5=makeQuery(id+"F9.imprint","IMPRINT",FACE,{"disambiguationData":[TD([[makeQuery(id+"F9.imprint","IMPRINT",EDGE,{"derivedFrom":sQuery(id+"F9.wireOp",EDGE,"E19.4.0")}),1.0]])]});
            var Q6;
            Q6=makeQuery(id+"F9.imprint","IMPRINT",FACE,{"disambiguationData":[TD([[makeQuery(id+"F9.imprint","IMPRINT",EDGE,{"derivedFrom":sQuery(id+"F9.wireOp",EDGE,"E19.5.0")}),1.0]])]});
            var Q7;
            Q7=makeQuery(id+"F9.imprint","IMPRINT",FACE,{"disambiguationData":[TD([[makeQuery(id+"F9.imprint","IMPRINT",EDGE,{"derivedFrom":sQuery(id+"F9.wireOp",EDGE,"E19.6.0")}),1.0]])]});
            var Q8;
            Q8=makeQuery(id+"F9.imprint","IMPRINT",FACE,{"disambiguationData":[TD([[makeQuery(id+"F9.imprint","IMPRINT",EDGE,{"derivedFrom":sQuery(id+"F9.wireOp",EDGE,"E19.7.0")}),1.0]])]});
            extrude(context, id + "F10", {"entities" : qUnion([Q0, Q1, Q2, Q3, Q4, Q5, Q6, Q7, Q8]), "operationType" : NewBodyOperationType.REMOVE, "oppositeDirection" : true, "depth" : 40 * mm});
        }
        {
            var Q0;
            Q0=makeQuery(id+"F7.opExtrude","CAP_FACE",FACE,{"disambiguationData":[OSD([sQuery(id+"F4.wireOp",EDGE,"E13")])],"isStart":false});
            var sketch = newSketch(context, id + "F11", { "sketchPlane" : qUnion([Q0])});
            skCircle(sketch, "E23", {"center": v(0, 0) * mm, "radius": 9 * mm});
            skLineSegment(sketch, "E24", {"start": v(0, 9) * mm, "end": v(0, 12) * mm, "construction": true});
            skCircle(sketch, "E25", {"center": v(0, 12) * mm, "radius": 1.3 * mm});
            skLineSegment(sketch, "E26.bottom", {"start": v(-4.15, 14.79) * mm, "end": v(-4.15, 14.79) * mm});
            skLineSegment(sketch, "E26.top", {"start": v(-4.15, 7.99) * mm, "end": v(-4.15, 7.99) * mm});
            skLineSegment(sketch, "E26.left", {"start": v(-4.15, 14.79) * mm, "end": v(-4.15, 7.99) * mm});
            skLineSegment(sketch, "E26.right", {"start": v(-4.15, 14.79) * mm, "end": v(-4.15, 7.99) * mm});
            skLineSegment(sketch, "E27", {"start": v(-4.15, 7.99) * mm, "end": v(4.15, 7.99) * mm});
            skLineSegment(sketch, "E28", {"start": v(4.15, 7.99) * mm, "end": v(4.15, 14.79) * mm});
            skLineSegment(sketch, "E29", {"start": v(4.15, 14.79) * mm, "end": v(-4.15, 14.79) * mm});
            skLineSegment(sketch, "E30.1.0", {"start": v(-14.79, 4.15) * mm, "end": v(-14.79, -4.15) * mm});
            skLineSegment(sketch, "E30.1.1", {"start": v(-14.79, -4.15) * mm, "end": v(-7.99, -4.15) * mm});
            skLineSegment(sketch, "E30.1.2", {"start": v(-7.99, 4.15) * mm, "end": v(-14.79, 4.15) * mm});
            skCircle(sketch, "E30.1.3", {"center": v(-12, 0) * mm, "radius": 1.3 * mm});
            skLineSegment(sketch, "E30.2.0", {"start": v(-4.15, -14.79) * mm, "end": v(4.15, -14.79) * mm});
            skLineSegment(sketch, "E30.2.1", {"start": v(4.15, -14.79) * mm, "end": v(4.15, -7.99) * mm});
            skLineSegment(sketch, "E30.2.2", {"start": v(-4.15, -7.99) * mm, "end": v(-4.15, -14.79) * mm});
            skCircle(sketch, "E30.2.3", {"center": v(0, -12) * mm, "radius": 1.3 * mm});
            skLineSegment(sketch, "E30.3.0", {"start": v(14.79, -4.15) * mm, "end": v(14.79, 4.15) * mm});
            skLineSegment(sketch, "E30.3.1", {"start": v(14.79, 4.15) * mm, "end": v(7.99, 4.15) * mm});
            skLineSegment(sketch, "E30.3.2", {"start": v(7.99, -4.15) * mm, "end": v(14.79, -4.15) * mm});
            skCircle(sketch, "E30.3.3", {"center": v(12, 0) * mm, "radius": 1.3 * mm});
            skSolve(sketch);
        }
        {
            var Q0;
            {var subQ0=sQuery(id+"F11.wireOp",EDGE,"E27");Q0=makeQuery(id+"F11.imprint","IMPRINT",FACE,{"disambiguationData":[TD([[makeQuery(id+"F11.imprint","IMPRINT",EDGE,{"derivedFrom":subQ0}),-1.0]])]});}
            var Q1;
            {var subQ0=sQuery(id+"F11.wireOp",EDGE,"E27");Q1=makeQuery(id+"F11.imprint","IMPRINT",FACE,{"disambiguationData":[TD([[makeQuery(id+"F11.imprint","IMPRINT",EDGE,{"derivedFrom":subQ0}),1.0]])]});}
            extrude(context, id + "F12", {"entities" : qUnion([Q0, Q1]), "operationType" : NewBodyOperationType.ADD, "depth" : 25.8 * mm});
        }
        {
            var Q0;
            Q0=makeQuery(id+"F11.imprint","IMPRINT",FACE,{"disambiguationData":[TD([[makeQuery(id+"F11.imprint","IMPRINT",EDGE,{"derivedFrom":sQuery(id+"F11.wireOp",EDGE,"E25")}),-1.0]])]});
            var Q1;
            Q1=makeQuery(id+"F11.imprint","IMPRINT",FACE,{"disambiguationData":[TD([[makeQuery(id+"F11.imprint","IMPRINT",EDGE,{"derivedFrom":sQuery(id+"F11.wireOp",EDGE,"E30.1.0")}),1.0]])]});
            var Q2;
            Q2=makeQuery(id+"F11.imprint","IMPRINT",FACE,{"disambiguationData":[TD([[makeQuery(id+"F11.imprint","IMPRINT",EDGE,{"derivedFrom":sQuery(id+"F11.wireOp",EDGE,"E30.3.0")}),1.0]])]});
            var Q3;
            Q3=makeQuery(id+"F11.imprint","IMPRINT",FACE,{"disambiguationData":[TD([[makeQuery(id+"F11.imprint","IMPRINT",EDGE,{"derivedFrom":sQuery(id+"F11.wireOp",EDGE,"E30.2.0")}),1.0]])]});
            extrude(context, id + "F13", {"entities" : qUnion([Q0, Q1, Q2, Q3]), "operationType" : NewBodyOperationType.ADD, "depth" : 17.1 * mm});
        }
        {
            var Q0;
            Q0=makeQuery(id+"F13.opExtrude","SWEPT_FACE",FACE,{"disambiguationData":[OSD([sQuery(id+"F11.wireOp",EDGE,"E28")])]});
            var sketch = newSketch(context, id + "F14", { "sketchPlane" : qUnion([Q0])});
            skLineSegment(sketch, "E31", {"start": v(-22.2, 14.79) * mm, "end": v(-18.3, 14.79) * mm, "construction": true});
            skLineSegment(sketch, "E32", {"start": v(-5.1, 14.79) * mm, "end": v(-5.1, 18.19) * mm, "construction": true});
            skLineSegment(sketch, "E33", {"start": v(-18.3, 14.79) * mm, "end": v(-5.1, 18.19) * mm});
            skLineSegment(sketch, "E34", {"start": v(-18.3, 14.79) * mm, "end": v(-5.1, 14.79) * mm});
            skLineSegment(sketch, "E35", {"start": v(-5.1, 14.79) * mm, "end": v(-5.1, 18.19) * mm});
            skSolve(sketch);
        }
        {
            var Q0;
            Q0=makeQuery(id+"F14.imprint","IMPRINT",FACE,{"disambiguationData":[TD([[makeQuery(id+"F14.imprint","IMPRINT",EDGE,{"derivedFrom":sQuery(id+"F14.wireOp",EDGE,"E33")}),-1.0]])]});
            extrude(context, id + "F15", {"entities" : qUnion([Q0]), "operationType" : NewBodyOperationType.ADD, "oppositeDirection" : true, "depth" : 1.4 * mm});
        }
        {
            var Q0;
            Q0=makeQuery(id+"F1.opExtrude","SWEPT_BODY",BODY,{"disambiguationData":[OSD([sQuery(id+"F0.wireOp",EDGE,"E0")])]});
            var Q1;
            Q1=qCreatedBy(makeId("Right.planeOp"),FACE);
            mirror(context, id + "F16", {"operationType" : NewBodyOperationType.ADD, "entities" : qUnion([Q0]), "mirrorPlane" : qUnion([Q1])});
        }
        {
            var Q0;
            Q0=makeQuery(id+"F16.opPattern","COPY",EDGE,{"derivedFrom":makeQuery(id+"F15.opExtrude","CAP_EDGE",EDGE,{"disambiguationData":[OSD([sQuery(id+"F14.wireOp",EDGE,"E33")])],"isStart":true}),"instanceName":"1"});
            var Q1;
            Q1=makeQuery(id+"F16.opPattern","COPY",EDGE,{"derivedFrom":makeQuery(id+"F15.opExtrude","CAP_EDGE",EDGE,{"disambiguationData":[OSD([sQuery(id+"F14.wireOp",EDGE,"E33")])],"isStart":false}),"instanceName":"1"});
            var Q2;
            Q2=makeQuery(id+"F15.opExtrude","CAP_EDGE",EDGE,{"disambiguationData":[OSD([sQuery(id+"F14.wireOp",EDGE,"E33")])],"isStart":false});
            var Q3;
            Q3=makeQuery(id+"F15.opExtrude","CAP_EDGE",EDGE,{"disambiguationData":[OSD([sQuery(id+"F14.wireOp",EDGE,"E33")])],"isStart":true});
            var Q4;
            Q4=makeQuery(id+"F13.opExtrude","CAP_EDGE",EDGE,{"disambiguationData":[OSD([sQuery(id+"F11.wireOp",EDGE,"E28")])],"isStart":false});
            var Q5;
            Q5=makeQuery(id+"F13.opExtrude","CAP_EDGE",EDGE,{"disambiguationData":[OSD([sQuery(id+"F11.wireOp",EDGE,"E26.right")])],"isStart":false});
            fillet(context, id + "F17", {"entities" : qUnion([Q0, Q1, Q2, Q3, Q4, Q5]), "radius" : 0.1 * mm, "tangentPropagation" : true, "allowEdgeOverflow" : false});
        }
        {
            var Q0;
            Q0=makeQuery(id+"F13.opExtrude","SWEPT_EDGE",EDGE,{"disambiguationData":[OSD([sQuery(id+"F11.wireOp",EDGE,"E26.right"),sQuery(id+"F11.wireOp",EDGE,"E29")])]});
            var Q1;
            Q1=makeQuery(id+"F13.opExtrude","SWEPT_EDGE",EDGE,{"disambiguationData":[OSD([sQuery(id+"F11.wireOp",EDGE,"E28"),sQuery(id+"F11.wireOp",EDGE,"E29")])]});
            fillet(context, id + "F18", {"entities" : qUnion([Q0, Q1]), "radius" : 0.1 * mm, "tangentPropagation" : true, "allowEdgeOverflow" : false});
        }
        {
            var Q0;
            Q0=makeQuery(id+"F13.opExtrude","SWEPT_FACE",FACE,{"disambiguationData":[OSD([sQuery(id+"F11.wireOp",EDGE,"E30.3.2")])]});
            var sketch = newSketch(context, id + "F19", { "sketchPlane" : qUnion([Q0])});
            skLineSegment(sketch, "E36", {"start": v(14.79, 22.2) * mm, "end": v(14.79, 18.3) * mm, "construction": true});
            skLineSegment(sketch, "E37", {"start": v(14.79, 5.1) * mm, "end": v(18.19, 5.1) * mm});
            skLineSegment(sketch, "E38", {"start": v(14.79, 18.3) * mm, "end": v(18.19, 5.1) * mm});
            skSolve(sketch);
        }
        {
            var Q0;
            {var subQ0=sQuery(id+"F19.wireOp",EDGE,"E37");Q0=makeQuery(id+"F19.imprint","IMPRINT",FACE,{"disambiguationData":[TD([[makeQuery(id+"F19.imprint","IMPRINT",EDGE,{"derivedFrom":subQ0}),1.0]])]});}
            extrude(context, id + "F20", {"entities" : qUnion([Q0]), "operationType" : NewBodyOperationType.ADD, "oppositeDirection" : true, "depth" : 1.4 * mm});
        }
        {
            var Q0;
            Q0=makeQuery(id+"F1.opExtrude","SWEPT_BODY",BODY,{"disambiguationData":[OSD([sQuery(id+"F0.wireOp",EDGE,"E0")])]});
            var Q1;
            Q1=qCreatedBy(makeId("Top.planeOp"),FACE);
            mirror(context, id + "F21", {"operationType" : NewBodyOperationType.ADD, "entities" : qUnion([Q0]), "mirrorPlane" : qUnion([Q1])});
        }
        {
            var Q0;
            Q0=makeQuery(id+"F13.opExtrude","CAP_EDGE",EDGE,{"disambiguationData":[OSD([sQuery(id+"F11.wireOp",EDGE,"E30.3.1")])],"isStart":false});
            var Q1;
            Q1=makeQuery(id+"F13.opExtrude","CAP_EDGE",EDGE,{"disambiguationData":[OSD([sQuery(id+"F11.wireOp",EDGE,"E30.3.2")])],"isStart":false});
            var Q2;
            Q2=makeQuery(id+"F21.opPattern","COPY",EDGE,{"derivedFrom":makeQuery(id+"F20.opExtrude","CAP_EDGE",EDGE,{"disambiguationData":[OSD([sQuery(id+"F19.wireOp",EDGE,"E38")])],"isStart":true}),"instanceName":"1"});
            var Q3;
            Q3=makeQuery(id+"F21.opPattern","COPY",EDGE,{"derivedFrom":makeQuery(id+"F20.opExtrude","CAP_EDGE",EDGE,{"disambiguationData":[OSD([sQuery(id+"F19.wireOp",EDGE,"E38")])],"isStart":false}),"instanceName":"1"});
            var Q4;
            Q4=makeQuery(id+"F20.opExtrude","CAP_EDGE",EDGE,{"disambiguationData":[OSD([sQuery(id+"F19.wireOp",EDGE,"E38")])],"isStart":false});
            var Q5;
            Q5=makeQuery(id+"F20.opExtrude","CAP_EDGE",EDGE,{"disambiguationData":[OSD([sQuery(id+"F19.wireOp",EDGE,"E38")])],"isStart":true});
            fillet(context, id + "F22", {"entities" : qUnion([Q0, Q1, Q2, Q3, Q4, Q5]), "radius" : 0.1 * mm, "tangentPropagation" : true, "allowEdgeOverflow" : false});
        }
        {
            var Q0;
            Q0=makeQuery(id+"F1.opExtrude","SWEPT_BODY",BODY,{"disambiguationData":[OSD([sQuery(id+"F0.wireOp",EDGE,"E0")])]});
            var Q1;
            Q1=qCreatedBy(makeId("Right.planeOp"),FACE);
            mirror(context, id + "F23", {"operationType" : NewBodyOperationType.ADD, "entities" : qUnion([Q0]), "mirrorPlane" : qUnion([Q1])});
        }
        {
            var Q0;
            Q0=makeQuery(id+"F12.opExtrude","CAP_FACE",FACE,{"disambiguationData":[OSD([sQuery(id+"F4.wireOp",EDGE,"E13"),sQuery(id+"F9.wireOp",EDGE,"E15"),sQuery(id+"F11.wireOp",EDGE,"E23")])],"isStart":false});
            var sketch = newSketch(context, id + "F24", { "sketchPlane" : qUnion([Q0])});
            skCircle(sketch, "E39.cCircle", {"center": v(0, 0) * mm, "radius": 9 * mm, "construction": true});
            skLineSegment(sketch, "E39.0", {"start": v(7.8, -4.5) * mm, "end": v(0, -9) * mm});
            skLineSegment(sketch, "E39.1", {"start": v(0, -9) * mm, "end": v(-7.8, -4.5) * mm});
            skLineSegment(sketch, "E39.2", {"start": v(-7.8, -4.5) * mm, "end": v(-7.8, 4.5) * mm});
            skLineSegment(sketch, "E39.3", {"start": v(-7.8, 4.5) * mm, "end": v(0, 9) * mm});
            skLineSegment(sketch, "E39.4", {"start": v(0, 9) * mm, "end": v(7.8, 4.5) * mm});
            skLineSegment(sketch, "E39.5", {"start": v(7.8, 4.5) * mm, "end": v(7.8, -4.5) * mm});
            skSolve(sketch);
        }
        {
            var Q0;
            Q0=makeQuery(id+"F24.imprint","IMPRINT",FACE,{"disambiguationData":[TD([[makeQuery(id+"F24.imprint","IMPRINT",EDGE,{"derivedFrom":sQuery(id+"F24.wireOp",EDGE,"E39.0")}),-1.0]])]});
            extrude(context, id + "F25", {"entities" : qUnion([Q0]), "operationType" : NewBodyOperationType.ADD, "depth" : 7.9 * mm});
        }
        {
            var Q0;
            Q0=makeQuery(id+"F25.opExtrude","CAP_FACE",FACE,{"disambiguationData":[OSD([sQuery(id+"F4.wireOp",EDGE,"E13"),sQuery(id+"F9.wireOp",EDGE,"E15"),sQuery(id+"F24.wireOp",EDGE,"E39.0"),sQuery(id+"F24.wireOp",EDGE,"E39.1"),sQuery(id+"F24.wireOp",EDGE,"E39.2"),sQuery(id+"F24.wireOp",EDGE,"E39.3"),sQuery(id+"F24.wireOp",EDGE,"E39.4"),sQuery(id+"F24.wireOp",EDGE,"E39.5")])],"isStart":false});
            var sketch = newSketch(context, id + "F26", { "sketchPlane" : qUnion([Q0])});
            skCircle(sketch, "E40", {"center": v(0, 0) * mm, "radius": 6.5 * mm});
            skSolve(sketch);
        }
        {
            var Q0;
            Q0=makeQuery(id+"F26.imprint","IMPRINT",FACE,{"disambiguationData":[TD([[makeQuery(id+"F26.imprint","IMPRINT",EDGE,{"derivedFrom":sQuery(id+"F26.wireOp",EDGE,"E40")}),1.0]])]});
            var Q1;
            Q1=sQuery(id+"F26.wireOp",EDGE,"E40");
            extrude(context, id + "F27", {"entities" : qUnion([Q0]), "operationType" : NewBodyOperationType.REMOVE, "surfaceEntities" : qUnion([Q1]), "oppositeDirection" : true, "depth" : 5.2 * mm});
        }
        {
            var Q0;
            Q0=makeQuery(id+"F3.boolean.opBoolean","MERGE",FACE,{"derivedFrom":[makeQuery(id+"F1.opExtrude","CAP_FACE",FACE,{"disambiguationData":[OSD([sQuery(id+"F0.wireOp",EDGE,"E0")])],"isStart":true}),makeQuery(id+"F3.opExtrude","CAP_FACE",FACE,{"disambiguationData":[OSD([sQuery(id+"F2.wireOp",EDGE,"E1"),sQuery(id+"F2.wireOp",EDGE,"E8"),sQuery(id+"F2.wireOp",EDGE,"E9"),sQuery(id+"F2.wireOp",EDGE,"E11"),sQuery(id+"F2.wireOp",EDGE,"E12.1.0"),sQuery(id+"F2.wireOp",EDGE,"E12.1.1"),sQuery(id+"F2.wireOp",EDGE,"E12.1.2"),sQuery(id+"F2.wireOp",EDGE,"E12.2.0"),sQuery(id+"F2.wireOp",EDGE,"E12.2.1"),sQuery(id+"F2.wireOp",EDGE,"E12.2.2"),sQuery(id+"F2.wireOp",EDGE,"E12.3.0"),sQuery(id+"F2.wireOp",EDGE,"E12.3.1"),sQuery(id+"F2.wireOp",EDGE,"E12.3.2"),sQuery(id+"F2.wireOp",EDGE,"E12.4.0"),sQuery(id+"F2.wireOp",EDGE,"E12.4.1"),sQuery(id+"F2.wireOp",EDGE,"E12.4.2"),sQuery(id+"F2.wireOp",EDGE,"E12.5.0"),sQuery(id+"F2.wireOp",EDGE,"E12.5.1"),sQuery(id+"F2.wireOp",EDGE,"E12.5.2"),sQuery(id+"F2.wireOp",EDGE,"E12.6.0"),sQuery(id+"F2.wireOp",EDGE,"E12.6.1"),sQuery(id+"F2.wireOp",EDGE,"E12.6.2"),sQuery(id+"F2.wireOp",EDGE,"E12.7.0"),sQuery(id+"F2.wireOp",EDGE,"E12.7.1"),sQuery(id+"F2.wireOp",EDGE,"E12.7.2"),sQuery(id+"F2.wireOp",EDGE,"E12.8.0"),sQuery(id+"F2.wireOp",EDGE,"E12.8.1"),sQuery(id+"F2.wireOp",EDGE,"E12.8.2"),sQuery(id+"F2.wireOp",EDGE,"E12.9.0"),sQuery(id+"F2.wireOp",EDGE,"E12.9.1"),sQuery(id+"F2.wireOp",EDGE,"E12.9.2"),sQuery(id+"F2.wireOp",EDGE,"E12.10.0"),sQuery(id+"F2.wireOp",EDGE,"E12.10.1"),sQuery(id+"F2.wireOp",EDGE,"E12.10.2"),sQuery(id+"F2.wireOp",EDGE,"E12.11.0"),sQuery(id+"F2.wireOp",EDGE,"E12.11.1"),sQuery(id+"F2.wireOp",EDGE,"E12.11.2"),sQuery(id+"F2.wireOp",EDGE,"E12.12.0"),sQuery(id+"F2.wireOp",EDGE,"E12.12.1"),sQuery(id+"F2.wireOp",EDGE,"E12.12.2"),sQuery(id+"F2.wireOp",EDGE,"E12.13.0"),sQuery(id+"F2.wireOp",EDGE,"E12.13.1"),sQuery(id+"F2.wireOp",EDGE,"E12.13.2"),sQuery(id+"F2.wireOp",EDGE,"E12.14.0"),sQuery(id+"F2.wireOp",EDGE,"E12.14.1"),sQuery(id+"F2.wireOp",EDGE,"E12.14.2"),sQuery(id+"F2.wireOp",EDGE,"E12.15.0"),sQuery(id+"F2.wireOp",EDGE,"E12.15.1"),sQuery(id+"F2.wireOp",EDGE,"E12.15.2"),sQuery(id+"F2.wireOp",EDGE,"E12.16.0"),sQuery(id+"F2.wireOp",EDGE,"E12.16.1"),sQuery(id+"F2.wireOp",EDGE,"E12.16.2"),sQuery(id+"F2.wireOp",EDGE,"E12.17.0"),sQuery(id+"F2.wireOp",EDGE,"E12.17.1"),sQuery(id+"F2.wireOp",EDGE,"E12.17.2"),sQuery(id+"F2.wireOp",EDGE,"E12.18.0"),sQuery(id+"F2.wireOp",EDGE,"E12.18.1"),sQuery(id+"F2.wireOp",EDGE,"E12.18.2"),sQuery(id+"F2.wireOp",EDGE,"E12.19.0"),sQuery(id+"F2.wireOp",EDGE,"E12.19.1"),sQuery(id+"F2.wireOp",EDGE,"E12.19.2"),sQuery(id+"F2.wireOp",EDGE,"E12.20.0"),sQuery(id+"F2.wireOp",EDGE,"E12.20.1"),sQuery(id+"F2.wireOp",EDGE,"E12.20.2"),sQuery(id+"F2.wireOp",EDGE,"E12.21.0"),sQuery(id+"F2.wireOp",EDGE,"E12.21.1"),sQuery(id+"F2.wireOp",EDGE,"E12.21.2"),sQuery(id+"F2.wireOp",EDGE,"E12.22.0"),sQuery(id+"F2.wireOp",EDGE,"E12.22.1"),sQuery(id+"F2.wireOp",EDGE,"E12.22.2"),sQuery(id+"F2.wireOp",EDGE,"E12.23.0"),sQuery(id+"F2.wireOp",EDGE,"E12.23.1"),sQuery(id+"F2.wireOp",EDGE,"E12.23.2"),sQuery(id+"F2.wireOp",EDGE,"E12.24.0"),sQuery(id+"F2.wireOp",EDGE,"E12.24.1"),sQuery(id+"F2.wireOp",EDGE,"E12.24.2"),sQuery(id+"F2.wireOp",EDGE,"E12.25.0"),sQuery(id+"F2.wireOp",EDGE,"E12.25.1"),sQuery(id+"F2.wireOp",EDGE,"E12.25.2")])],"isStart":true})]});
            var sketch = newSketch(context, id + "F28", { "sketchPlane" : qUnion([Q0])});
            skCircle(sketch, "E41", {"center": v(0, 0) * mm, "radius": 6.5 * mm});
            skSolve(sketch);
        }
        {
            var Q0;
            Q0=makeQuery(id+"F28.imprint","IMPRINT",FACE,{"disambiguationData":[TD([[makeQuery(id+"F28.imprint","IMPRINT",EDGE,{"derivedFrom":sQuery(id+"F28.wireOp",EDGE,"E41")}),1.0]])]});
            extrude(context, id + "F29", {"entities" : qUnion([Q0]), "operationType" : NewBodyOperationType.REMOVE, "oppositeDirection" : true, "depth" : 5 * mm});
        }
        {
            var Q0;
            Q0=makeQuery(id+"F25.opExtrude","CAP_FACE",FACE,{"disambiguationData":[OSD([sQuery(id+"F4.wireOp",EDGE,"E13"),sQuery(id+"F9.wireOp",EDGE,"E15"),sQuery(id+"F24.wireOp",EDGE,"E39.0"),sQuery(id+"F24.wireOp",EDGE,"E39.1"),sQuery(id+"F24.wireOp",EDGE,"E39.2"),sQuery(id+"F24.wireOp",EDGE,"E39.3"),sQuery(id+"F24.wireOp",EDGE,"E39.4"),sQuery(id+"F24.wireOp",EDGE,"E39.5")])],"isStart":false});
            fillet(context, id + "F30", {"entities" : qUnion([Q0]), "radius" : 0.2 * mm, "tangentPropagation" : true, "allowEdgeOverflow" : false});
        }
        {
            var Q0;
            Q0=makeQuery(id+"F25.opExtrude","SWEPT_EDGE",EDGE,{"disambiguationData":[OSD([sQuery(id+"F11.wireOp",EDGE,"E23"),sQuery(id+"F24.wireOp",EDGE,"E39.2"),sQuery(id+"F24.wireOp",EDGE,"E39.3")])]});
            var Q1;
            Q1=makeQuery(id+"F25.opExtrude","SWEPT_EDGE",EDGE,{"disambiguationData":[OSD([sQuery(id+"F11.wireOp",EDGE,"E23"),sQuery(id+"F24.wireOp",EDGE,"E39.1"),sQuery(id+"F24.wireOp",EDGE,"E39.2")])]});
            var Q2;
            Q2=makeQuery(id+"F25.opExtrude","SWEPT_EDGE",EDGE,{"disambiguationData":[OSD([sQuery(id+"F11.wireOp",EDGE,"E23"),sQuery(id+"F24.wireOp",EDGE,"E39.0"),sQuery(id+"F24.wireOp",EDGE,"E39.1")])]});
            var Q3;
            Q3=makeQuery(id+"F25.opExtrude","SWEPT_EDGE",EDGE,{"disambiguationData":[OSD([sQuery(id+"F11.wireOp",EDGE,"E23"),sQuery(id+"F24.wireOp",EDGE,"E39.0"),sQuery(id+"F24.wireOp",EDGE,"E39.5")])]});
            var Q4;
            Q4=makeQuery(id+"F25.opExtrude","SWEPT_EDGE",EDGE,{"disambiguationData":[OSD([sQuery(id+"F11.wireOp",EDGE,"E23"),sQuery(id+"F24.wireOp",EDGE,"E39.4"),sQuery(id+"F24.wireOp",EDGE,"E39.5")])]});
            var Q5;
            Q5=makeQuery(id+"F25.opExtrude","SWEPT_EDGE",EDGE,{"disambiguationData":[OSD([sQuery(id+"F11.wireOp",EDGE,"E23"),sQuery(id+"F24.wireOp",EDGE,"E39.3"),sQuery(id+"F24.wireOp",EDGE,"E39.4")])]});
            fillet(context, id + "F31", {"entities" : qUnion([Q0, Q1, Q2, Q3, Q4, Q5]), "radius" : 0.2 * mm, "tangentPropagation" : true, "allowEdgeOverflow" : false});
        }
    });
